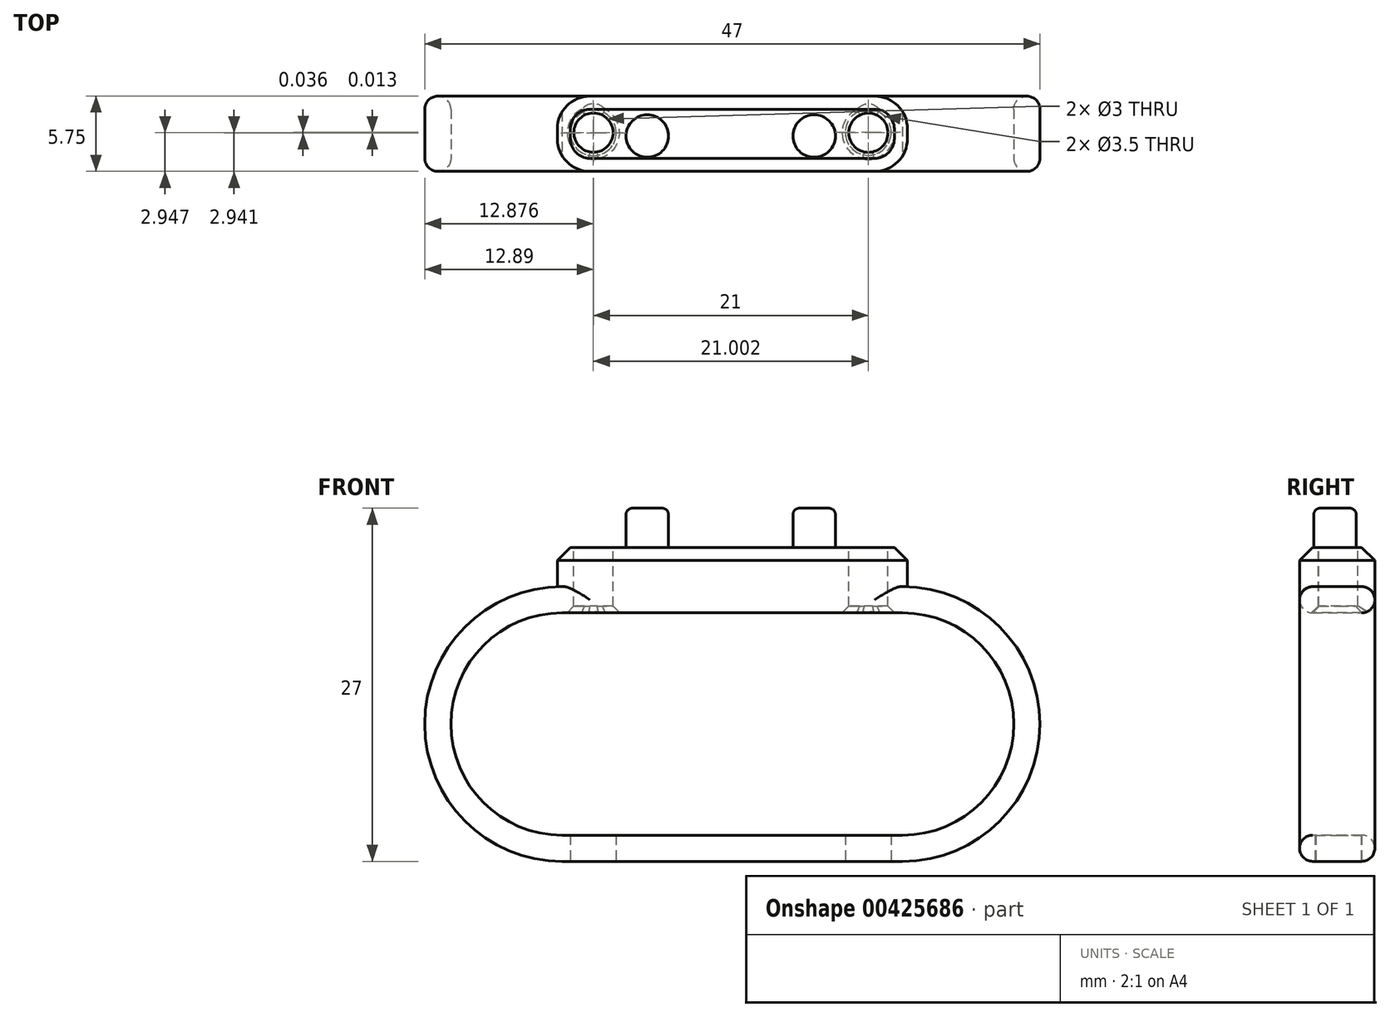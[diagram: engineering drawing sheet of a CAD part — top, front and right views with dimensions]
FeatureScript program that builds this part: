
annotation { "Feature Type Name" : "Feature", "Feature Type Description" : "" }
export const myFeature = defineFeature(function(context is Context, id is Id, definition is map)
    precondition{}
    {
        {
            var Q0;
            Q0=qCreatedBy(makeId("Top.planeOp"),FACE);
            var sketch = newSketch(context, id + "F0", { "sketchPlane" : qUnion([Q0])});
            skLineSegment(sketch, "E0.bottom", {"start": v(-13.87, 11.47) * mm, "end": v(7.88, 11.47) * mm});
            skLineSegment(sketch, "E0.top", {"start": v(-13.87, 5.72) * mm, "end": v(7.88, 5.72) * mm});
            skLineSegment(sketch, "E0.left", {"start": v(-16.37, 8.97) * mm, "end": v(-16.37, 8.22) * mm});
            skLineSegment(sketch, "E0.right", {"start": v(10.38, 8.97) * mm, "end": v(10.38, 8.22) * mm});
            skPoint(sketch, "E1.visualSharp", {"position": v(-16.37, 11.47) * mm});
            skArc(sketch, "E1.filletArc", {"start": v(-13.87, 11.47) * mm, "mid": v(-15.63, 10.73) * mm, "end": v(-16.37, 8.97) * mm});
            skPoint(sketch, "E2.visualSharp", {"position": v(-16.37, 5.72) * mm});
            skArc(sketch, "E2.filletArc", {"start": v(-16.37, 8.22) * mm, "mid": v(-15.63, 6.45) * mm, "end": v(-13.87, 5.72) * mm});
            skPoint(sketch, "E3.visualSharp", {"position": v(10.38, 5.72) * mm});
            skArc(sketch, "E3.filletArc", {"start": v(7.88, 5.72) * mm, "mid": v(9.65, 6.45) * mm, "end": v(10.38, 8.22) * mm});
            skPoint(sketch, "E4.visualSharp", {"position": v(10.38, 11.47) * mm});
            skArc(sketch, "E4.filletArc", {"start": v(10.38, 8.97) * mm, "mid": v(9.65, 10.73) * mm, "end": v(7.88, 11.47) * mm});
            skSolve(sketch);
        }
        {
            var Q0;
            Q0=makeQuery(id+"F0.imprint","IMPRINT",FACE,{"disambiguationData":[TD([[makeQuery(id+"F0.imprint","IMPRINT",EDGE,{"derivedFrom":sQuery(id+"F0.wireOp",EDGE,"E0.bottom")}),-1.0]])]});
            extrude(context, id + "F1", {"entities" : qUnion([Q0]), "depth" : 3 * mm});
        }
        {
            var Q0;
            Q0=makeQuery(id+"F1.opExtrude","CAP_FACE",FACE,{"disambiguationData":[OSD([sQuery(id+"F0.wireOp",EDGE,"E0.bottom"),sQuery(id+"F0.wireOp",EDGE,"E0.top"),sQuery(id+"F0.wireOp",EDGE,"E0.left"),sQuery(id+"F0.wireOp",EDGE,"E0.right"),sQuery(id+"F0.wireOp",EDGE,"E1.filletArc"),sQuery(id+"F0.wireOp",EDGE,"E2.filletArc"),sQuery(id+"F0.wireOp",EDGE,"E3.filletArc"),sQuery(id+"F0.wireOp",EDGE,"E4.filletArc")])],"isStart":false});
            var sketch = newSketch(context, id + "F2", { "sketchPlane" : qUnion([Q0])});
            skCircle(sketch, "E5", {"center": v(-9.49, 8.42) * mm, "radius": 1.63 * mm});
            skCircle(sketch, "E6", {"center": v(3.26, 8.42) * mm, "radius": 1.63 * mm});
            skCircle(sketch, "E7", {"center": v(7.4, 8.67) * mm, "radius": 1.5 * mm});
            skCircle(sketch, "E8", {"center": v(-13.6, 8.68) * mm, "radius": 1.5 * mm});
            skSolve(sketch);
        }
        {
            var Q0;
            Q0=makeQuery(id+"F2.imprint","IMPRINT",FACE,{"disambiguationData":[TD([[makeQuery(id+"F2.imprint","IMPRINT",EDGE,{"derivedFrom":sQuery(id+"F2.wireOp",EDGE,"E5")}),1.0]])]});
            var Q1;
            Q1=makeQuery(id+"F2.imprint","IMPRINT",FACE,{"disambiguationData":[TD([[makeQuery(id+"F2.imprint","IMPRINT",EDGE,{"derivedFrom":sQuery(id+"F2.wireOp",EDGE,"E6")}),1.0]])]});
            extrude(context, id + "F3", {"entities" : qUnion([Q0, Q1]), "operationType" : NewBodyOperationType.ADD, "depth" : 3 * mm});
        }
        {
            var Q0;
            Q0=makeQuery(id+"F3.opExtrude","CAP_FACE",FACE,{"disambiguationData":[OSD([sQuery(id+"F2.wireOp",EDGE,"E6")])],"isStart":false});
            var Q1;
            Q1=makeQuery(id+"F3.opExtrude","CAP_FACE",FACE,{"disambiguationData":[OSD([sQuery(id+"F2.wireOp",EDGE,"E5")])],"isStart":false});
            fillet(context, id + "F4", {"entities" : qUnion([Q0, Q1]), "radius" : 0.5 * mm, "tangentPropagation" : true, "allowEdgeOverflow" : false});
        }
        {
            var Q0;
            Q0=makeQuery(id+"F1.opExtrude","CAP_EDGE",EDGE,{"disambiguationData":[OSD([sQuery(id+"F0.wireOp",EDGE,"E0.bottom")])],"isStart":false});
            var Q1;
            Q1=makeQuery(id+"F1.opExtrude","CAP_EDGE",EDGE,{"disambiguationData":[OSD([sQuery(id+"F0.wireOp",EDGE,"E4.filletArc")])],"isStart":false});
            var Q2;
            Q2=makeQuery(id+"F1.opExtrude","CAP_EDGE",EDGE,{"disambiguationData":[OSD([sQuery(id+"F0.wireOp",EDGE,"E1.filletArc")])],"isStart":false});
            var Q3;
            Q3=makeQuery(id+"F1.opExtrude","CAP_EDGE",EDGE,{"disambiguationData":[OSD([sQuery(id+"F0.wireOp",EDGE,"E0.right")])],"isStart":false});
            var Q4;
            Q4=makeQuery(id+"F1.opExtrude","CAP_EDGE",EDGE,{"disambiguationData":[OSD([sQuery(id+"F0.wireOp",EDGE,"E3.filletArc")])],"isStart":false});
            var Q5;
            Q5=makeQuery(id+"F1.opExtrude","CAP_EDGE",EDGE,{"disambiguationData":[OSD([sQuery(id+"F0.wireOp",EDGE,"E0.top")])],"isStart":false});
            var Q6;
            Q6=makeQuery(id+"F1.opExtrude","CAP_EDGE",EDGE,{"disambiguationData":[OSD([sQuery(id+"F0.wireOp",EDGE,"E0.left")])],"isStart":false});
            var Q7;
            Q7=makeQuery(id+"F1.opExtrude","CAP_EDGE",EDGE,{"disambiguationData":[OSD([sQuery(id+"F0.wireOp",EDGE,"E2.filletArc")])],"isStart":false});
            chamfer(context, id + "F5", {"entities" : qUnion([Q0, Q1, Q2, Q3, Q4, Q5, Q6, Q7]), "width" : 1 * mm, "tangentPropagation" : true});
        }
        {
            var Q0;
            Q0=makeQuery(id+"F1.opExtrude","SWEPT_FACE",FACE,{"disambiguationData":[OSD([sQuery(id+"F0.wireOp",EDGE,"E0.top")])]});
            var sketch = newSketch(context, id + "F6", { "sketchPlane" : qUnion([Q0])});
            skPoint(sketch, "E9", {"position": v(-3, 0) * mm});
            skLineSegment(sketch, "E10", {"start": v(-16, 0) * mm, "end": v(10, 0) * mm});
            skLineSegment(sketch, "E11", {"start": v(10, -21) * mm, "end": v(-16, -21) * mm});
            skPoint(sketch, "E12", {"position": v(-3, -21) * mm});
            skArc(sketch, "E13", {"start": v(10, 0) * mm, "mid": v(20.5, -10.5) * mm, "end": v(10, -21) * mm});
            skArc(sketch, "E14", {"start": v(-16, 0) * mm, "mid": v(-26.5, -10.5) * mm, "end": v(-16, -21) * mm});
            skSolve(sketch);
        }
        {
            var Q0;
            Q0 = qSketchRegion(id + "F6", true);
            extrude(context, id + "F7", {"entities" : qUnion([Q0]), "operationType" : NewBodyOperationType.ADD, "oppositeDirection" : true, "depth" : 5.75 * mm});
        }
        {
            var Q0;
            Q0=makeQuery(id+"F7.boolean.opBoolean","MERGE",FACE,{"derivedFrom":[makeQuery(id+"F1.opExtrude","SWEPT_FACE",FACE,{"disambiguationData":[OSD([sQuery(id+"F0.wireOp",EDGE,"E0.top")])]}),makeQuery(id+"F7.opExtrude","CAP_FACE",FACE,{"disambiguationData":[OSD([sQuery(id+"F6.wireOp",EDGE,"E10"),sQuery(id+"F6.wireOp",EDGE,"E11"),sQuery(id+"F6.wireOp",EDGE,"E13"),sQuery(id+"F6.wireOp",EDGE,"E14")])],"isStart":true})]});
            var sketch = newSketch(context, id + "F8", { "sketchPlane" : qUnion([Q0])});
            skLineSegment(sketch, "E15.0", {"start": v(10, -2) * mm, "end": v(5.88, -2) * mm});
            skArc(sketch, "E15.1", {"start": v(10, -19) * mm, "mid": v(18.5, -10.5) * mm, "end": v(10, -2) * mm});
            skLineSegment(sketch, "E15.3", {"start": v(-16, -19) * mm, "end": v(10, -19) * mm});
            skLineSegment(sketch, "E15.6", {"start": v(-11.87, -2) * mm, "end": v(-16, -2) * mm});
            skArc(sketch, "E15.7", {"start": v(-16, -2) * mm, "mid": v(-24.5, -10.5) * mm, "end": v(-16, -19) * mm});
            skLineSegment(sketch, "E16", {"start": v(-11.87, -2) * mm, "end": v(5.88, -2) * mm});
            skSolve(sketch);
        }
        {
            var Q0;
            Q0=makeQuery(id+"F8.imprint","IMPRINT",FACE,{"disambiguationData":[TD([[makeQuery(id+"F8.imprint","IMPRINT",EDGE,{"derivedFrom":sQuery(id+"F8.wireOp",EDGE,"E15.0")}),1.0]])]});
            extrude(context, id + "F9", {"entities" : qUnion([Q0]), "operationType" : NewBodyOperationType.REMOVE, "endBound" : BoundingType.SYMMETRIC, "oppositeDirection" : true, "depth" : 25 * mm});
        }
        {
            var Q0;
            Q0=makeQuery(id+"F9.boolean.opBoolean","INTERSECT",EDGE,{"derivedFrom":[makeQuery(id+"F7.boolean.opBoolean","MERGE",FACE,{"derivedFrom":[makeQuery(id+"F1.opExtrude","SWEPT_FACE",FACE,{"disambiguationData":[OSD([sQuery(id+"F0.wireOp",EDGE,"E0.top")])]}),makeQuery(id+"F7.opExtrude","CAP_FACE",FACE,{"disambiguationData":[OSD([sQuery(id+"F6.wireOp",EDGE,"E10"),sQuery(id+"F6.wireOp",EDGE,"E11"),sQuery(id+"F6.wireOp",EDGE,"E13"),sQuery(id+"F6.wireOp",EDGE,"E14")])],"isStart":true})]}),makeQuery(id+"F9.opExtrude","SWEPT_FACE",FACE,{"disambiguationData":[OSD([sQuery(id+"F8.wireOp",EDGE,"E15.7")])]})]});
            var Q1;
            Q1=makeQuery(id+"F9.boolean.opBoolean","INTERSECT",EDGE,{"derivedFrom":[makeQuery(id+"F7.boolean.opBoolean","MERGE",FACE,{"derivedFrom":[makeQuery(id+"F1.opExtrude","SWEPT_FACE",FACE,{"disambiguationData":[OSD([sQuery(id+"F0.wireOp",EDGE,"E0.top")])]}),makeQuery(id+"F7.opExtrude","CAP_FACE",FACE,{"disambiguationData":[OSD([sQuery(id+"F6.wireOp",EDGE,"E10"),sQuery(id+"F6.wireOp",EDGE,"E11"),sQuery(id+"F6.wireOp",EDGE,"E13"),sQuery(id+"F6.wireOp",EDGE,"E14")])],"isStart":true})]}),makeQuery(id+"F9.opExtrude","SWEPT_FACE",FACE,{"disambiguationData":[OSD([sQuery(id+"F8.wireOp",EDGE,"E15.1")])]})]});
            var Q2;
            Q2=makeQuery(id+"F9.boolean.opBoolean","INTERSECT",EDGE,{"derivedFrom":[makeQuery(id+"F7.boolean.opBoolean","MERGE",FACE,{"derivedFrom":[makeQuery(id+"F1.opExtrude","SWEPT_FACE",FACE,{"disambiguationData":[OSD([sQuery(id+"F0.wireOp",EDGE,"E0.top")])]}),makeQuery(id+"F7.opExtrude","CAP_FACE",FACE,{"disambiguationData":[OSD([sQuery(id+"F6.wireOp",EDGE,"E10"),sQuery(id+"F6.wireOp",EDGE,"E11"),sQuery(id+"F6.wireOp",EDGE,"E13"),sQuery(id+"F6.wireOp",EDGE,"E14")])],"isStart":true})]}),makeQuery(id+"F9.opExtrude","SWEPT_FACE",FACE,{"disambiguationData":[OSD([sQuery(id+"F8.wireOp",EDGE,"E15.3")])]})]});
            var Q3;
            Q3=makeQuery(id+"F7.opExtrude","CAP_EDGE",EDGE,{"disambiguationData":[OSD([sQuery(id+"F6.wireOp",EDGE,"E14")])],"isStart":true});
            var Q4;
            Q4=makeQuery(id+"F7.opExtrude","CAP_EDGE",EDGE,{"disambiguationData":[OSD([sQuery(id+"F6.wireOp",EDGE,"E13")])],"isStart":true});
            var Q5;
            Q5=makeQuery(id+"F7.opExtrude","CAP_EDGE",EDGE,{"disambiguationData":[OSD([sQuery(id+"F6.wireOp",EDGE,"E11")])],"isStart":true});
            var Q6;
            Q6=makeQuery(id+"F7.opExtrude","CAP_EDGE",EDGE,{"disambiguationData":[OSD([sQuery(id+"F6.wireOp",EDGE,"E13")])],"isStart":false});
            var Q7;
            Q7=makeQuery(id+"F9.boolean.opBoolean","INTERSECT",EDGE,{"derivedFrom":[makeQuery(id+"F7.boolean.opBoolean","MERGE",FACE,{"derivedFrom":[makeQuery(id+"F1.opExtrude","SWEPT_FACE",FACE,{"disambiguationData":[OSD([sQuery(id+"F0.wireOp",EDGE,"E0.bottom")])]}),makeQuery(id+"F7.opExtrude","CAP_FACE",FACE,{"disambiguationData":[OSD([sQuery(id+"F6.wireOp",EDGE,"E10"),sQuery(id+"F6.wireOp",EDGE,"E11"),sQuery(id+"F6.wireOp",EDGE,"E13"),sQuery(id+"F6.wireOp",EDGE,"E14")])],"isStart":false})]}),makeQuery(id+"F9.opExtrude","SWEPT_FACE",FACE,{"disambiguationData":[OSD([sQuery(id+"F8.wireOp",EDGE,"E15.1")])]})]});
            var Q8;
            Q8=makeQuery(id+"F9.boolean.opBoolean","INTERSECT",EDGE,{"derivedFrom":[makeQuery(id+"F7.boolean.opBoolean","MERGE",FACE,{"derivedFrom":[makeQuery(id+"F1.opExtrude","SWEPT_FACE",FACE,{"disambiguationData":[OSD([sQuery(id+"F0.wireOp",EDGE,"E0.bottom")])]}),makeQuery(id+"F7.opExtrude","CAP_FACE",FACE,{"disambiguationData":[OSD([sQuery(id+"F6.wireOp",EDGE,"E10"),sQuery(id+"F6.wireOp",EDGE,"E11"),sQuery(id+"F6.wireOp",EDGE,"E13"),sQuery(id+"F6.wireOp",EDGE,"E14")])],"isStart":false})]}),makeQuery(id+"F9.opExtrude","SWEPT_FACE",FACE,{"disambiguationData":[OSD([sQuery(id+"F8.wireOp",EDGE,"E15.0"),sQuery(id+"F8.wireOp",EDGE,"E15.6"),sQuery(id+"F8.wireOp",EDGE,"E16")])]})]});
            var Q9;
            Q9=makeQuery(id+"F9.boolean.opBoolean","INTERSECT",EDGE,{"derivedFrom":[makeQuery(id+"F7.boolean.opBoolean","MERGE",FACE,{"derivedFrom":[makeQuery(id+"F1.opExtrude","SWEPT_FACE",FACE,{"disambiguationData":[OSD([sQuery(id+"F0.wireOp",EDGE,"E0.bottom")])]}),makeQuery(id+"F7.opExtrude","CAP_FACE",FACE,{"disambiguationData":[OSD([sQuery(id+"F6.wireOp",EDGE,"E10"),sQuery(id+"F6.wireOp",EDGE,"E11"),sQuery(id+"F6.wireOp",EDGE,"E13"),sQuery(id+"F6.wireOp",EDGE,"E14")])],"isStart":false})]}),makeQuery(id+"F9.opExtrude","SWEPT_FACE",FACE,{"disambiguationData":[OSD([sQuery(id+"F8.wireOp",EDGE,"E15.7")])]})]});
            var Q10;
            Q10=makeQuery(id+"F9.boolean.opBoolean","INTERSECT",EDGE,{"derivedFrom":[makeQuery(id+"F7.boolean.opBoolean","MERGE",FACE,{"derivedFrom":[makeQuery(id+"F1.opExtrude","SWEPT_FACE",FACE,{"disambiguationData":[OSD([sQuery(id+"F0.wireOp",EDGE,"E0.bottom")])]}),makeQuery(id+"F7.opExtrude","CAP_FACE",FACE,{"disambiguationData":[OSD([sQuery(id+"F6.wireOp",EDGE,"E10"),sQuery(id+"F6.wireOp",EDGE,"E11"),sQuery(id+"F6.wireOp",EDGE,"E13"),sQuery(id+"F6.wireOp",EDGE,"E14")])],"isStart":false})]}),makeQuery(id+"F9.opExtrude","SWEPT_FACE",FACE,{"disambiguationData":[OSD([sQuery(id+"F8.wireOp",EDGE,"E15.3")])]})]});
            var Q11;
            Q11=makeQuery(id+"F7.opExtrude","CAP_EDGE",EDGE,{"disambiguationData":[OSD([sQuery(id+"F6.wireOp",EDGE,"E11")])],"isStart":false});
            var Q12;
            Q12=makeQuery(id+"F9.boolean.opBoolean","INTERSECT",EDGE,{"derivedFrom":[makeQuery(id+"F7.boolean.opBoolean","MERGE",FACE,{"derivedFrom":[makeQuery(id+"F1.opExtrude","SWEPT_FACE",FACE,{"disambiguationData":[OSD([sQuery(id+"F0.wireOp",EDGE,"E0.top")])]}),makeQuery(id+"F7.opExtrude","CAP_FACE",FACE,{"disambiguationData":[OSD([sQuery(id+"F6.wireOp",EDGE,"E10"),sQuery(id+"F6.wireOp",EDGE,"E11"),sQuery(id+"F6.wireOp",EDGE,"E13"),sQuery(id+"F6.wireOp",EDGE,"E14")])],"isStart":true})]}),makeQuery(id+"F9.opExtrude","SWEPT_FACE",FACE,{"disambiguationData":[OSD([sQuery(id+"F8.wireOp",EDGE,"E15.0"),sQuery(id+"F8.wireOp",EDGE,"E15.6"),sQuery(id+"F8.wireOp",EDGE,"E16")])]})]});
            fillet(context, id + "F10", {"entities" : qUnion([Q0, Q1, Q2, Q3, Q4, Q5, Q6, Q7, Q8, Q9, Q10, Q11, Q12]), "radius" : 1 * mm, "tangentPropagation" : true, "allowEdgeOverflow" : false});
        }
        {
            var Q0;
            Q0=makeQuery(id+"F2.imprint","IMPRINT",FACE,{"disambiguationData":[TD([[makeQuery(id+"F2.imprint","IMPRINT",EDGE,{"derivedFrom":sQuery(id+"F2.wireOp",EDGE,"E7")}),1.0]])]});
            var Q1;
            Q1=makeQuery(id+"F2.imprint","IMPRINT",FACE,{"disambiguationData":[TD([[makeQuery(id+"F2.imprint","IMPRINT",EDGE,{"derivedFrom":sQuery(id+"F2.wireOp",EDGE,"E8")}),1.0]])]});
            extrude(context, id + "F11", {"entities" : qUnion([Q0, Q1]), "operationType" : NewBodyOperationType.REMOVE, "endBound" : BoundingType.SYMMETRIC, "oppositeDirection" : true, "depth" : 25 * mm});
        }
        {
            var Q0;
            Q0=makeQuery(id+"F11.boolean.opBoolean","INTERSECT",EDGE,{"derivedFrom":[makeQuery(id+"F9.boolean.opBoolean","COPY",FACE,{"derivedFrom":makeQuery(id+"F9.opExtrude","SWEPT_FACE",FACE,{"disambiguationData":[OSD([sQuery(id+"F8.wireOp",EDGE,"E15.0"),sQuery(id+"F8.wireOp",EDGE,"E15.6"),sQuery(id+"F8.wireOp",EDGE,"E16")])]})}),makeQuery(id+"F11.opExtrude","SWEPT_FACE",FACE,{"disambiguationData":[OSD([sQuery(id+"F2.wireOp",EDGE,"E7")])]})]});
            var Q1;
            Q1=makeQuery(id+"F11.boolean.opBoolean","INTERSECT",EDGE,{"derivedFrom":[makeQuery(id+"F9.boolean.opBoolean","COPY",FACE,{"derivedFrom":makeQuery(id+"F9.opExtrude","SWEPT_FACE",FACE,{"disambiguationData":[OSD([sQuery(id+"F8.wireOp",EDGE,"E15.0"),sQuery(id+"F8.wireOp",EDGE,"E15.6"),sQuery(id+"F8.wireOp",EDGE,"E16")])]})}),makeQuery(id+"F11.opExtrude","SWEPT_FACE",FACE,{"disambiguationData":[OSD([sQuery(id+"F2.wireOp",EDGE,"E8")])]})]});
            chamfer(context, id + "F12", {"entities" : qUnion([Q0, Q1]), "width" : .5 * mm, "tangentPropagation" : true});
        }
        {
            var Q0;
            Q0=makeQuery(id+"F7.opExtrude","SWEPT_FACE",FACE,{"disambiguationData":[OSD([sQuery(id+"F6.wireOp",EDGE,"E11")])]});
            var sketch = newSketch(context, id + "F13", { "sketchPlane" : qUnion([Q0])});
            skCircle(sketch, "E17", {"center": v(-13.61, -8.66) * mm, "radius": 1.75 * mm});
            skCircle(sketch, "E18", {"center": v(7.39, -8.7) * mm, "radius": 1.75 * mm});
            skSolve(sketch);
        }
        {
            var Q0;
            Q0=makeQuery(id+"F13.imprint","IMPRINT",FACE,{"disambiguationData":[TD([[makeQuery(id+"F13.imprint","IMPRINT",EDGE,{"derivedFrom":sQuery(id+"F13.wireOp",EDGE,"E18")}),1.0]])]});
            var Q1;
            Q1=makeQuery(id+"F13.imprint","IMPRINT",FACE,{"disambiguationData":[TD([[makeQuery(id+"F13.imprint","IMPRINT",EDGE,{"derivedFrom":sQuery(id+"F13.wireOp",EDGE,"E17")}),1.0]])]});
            extrude(context, id + "F14", {"entities" : qUnion([Q0, Q1]), "operationType" : NewBodyOperationType.REMOVE, "endBound" : BoundingType.SYMMETRIC, "oppositeDirection" : true, "depth" : 15 * mm});
        }
    });
